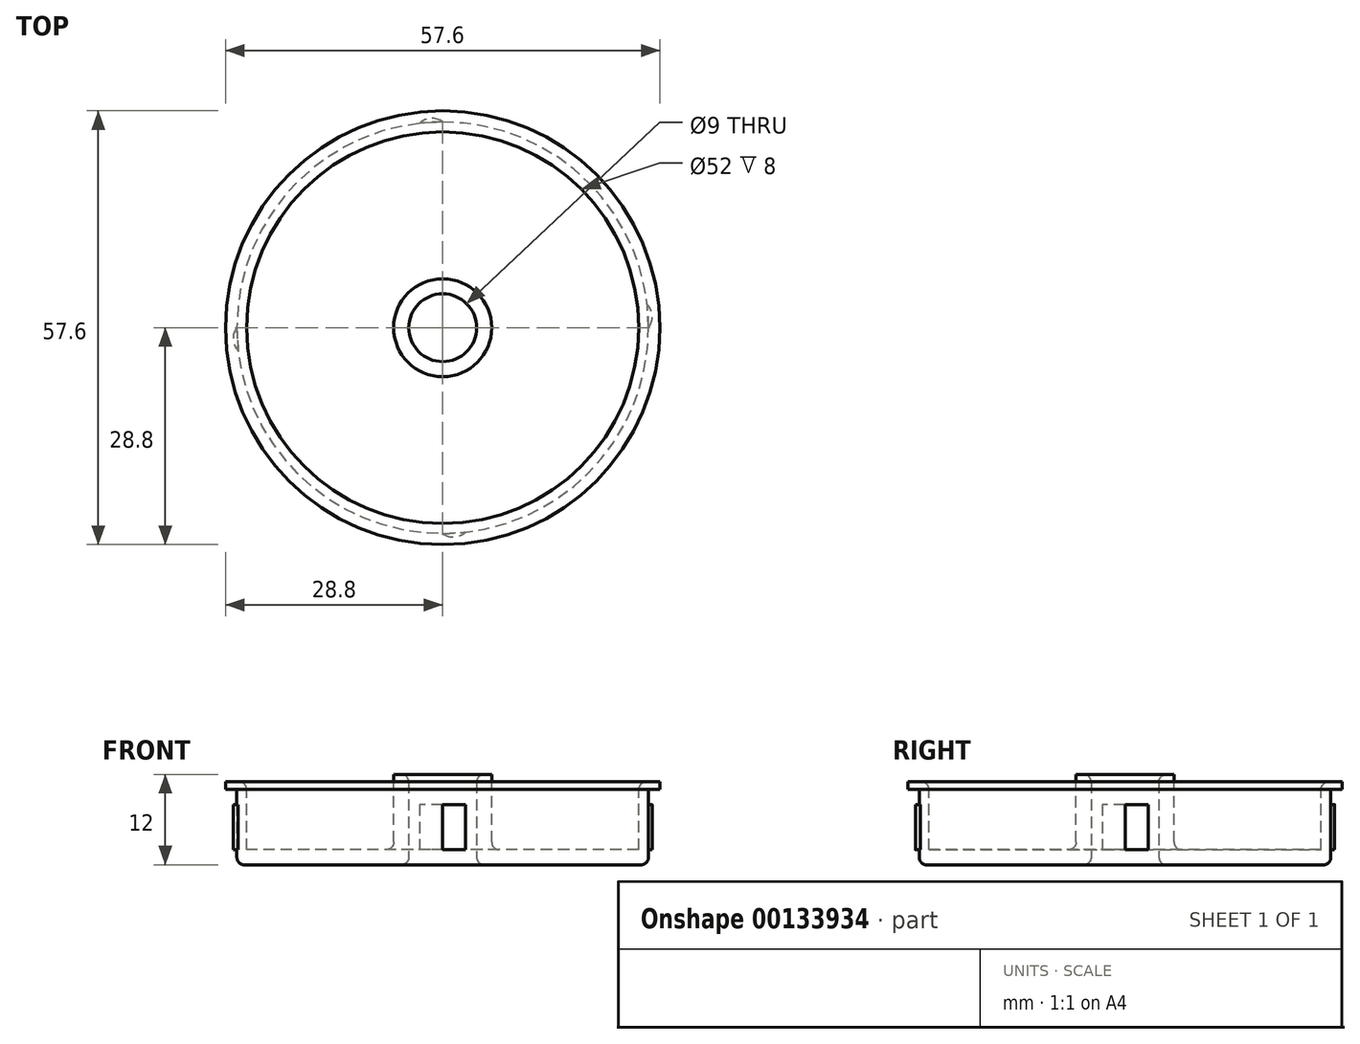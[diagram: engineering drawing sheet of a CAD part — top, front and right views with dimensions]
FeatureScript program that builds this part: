
annotation { "Feature Type Name" : "Feature", "Feature Type Description" : "" }
export const myFeature = defineFeature(function(context is Context, id is Id, definition is map)
    precondition{}
    {
        {
            var Q0;
            Q0=qCreatedBy(makeId("Top.planeOp"),FACE);
            var sketch = newSketch(context, id + "F0", { "sketchPlane" : qUnion([Q0])});
            skCircle(sketch, "E0", {"center": v(0, 0) * mm, "radius": 27.3 * mm});
            skCircle(sketch, "E1", {"center": v(0, 0) * mm, "radius": 4.5 * mm});
            skSolve(sketch);
        }
        {
            var Q0;
            Q0 = qSketchRegion(id + "F0", true);
            extrude(context, id + "F1", {"entities" : qUnion([Q0]), "depth" : 10 * mm});
        }
        {
            var Q0;
            Q0=makeQuery(id+"F1.opExtrude","CAP_FACE",FACE,{"disambiguationData":[OSD([sQuery(id+"F0.wireOp",EDGE,"E0"),sQuery(id+"F0.wireOp",EDGE,"E1")])],"isStart":false});
            var sketch = newSketch(context, id + "F2", { "sketchPlane" : qUnion([Q0])});
            skCircle(sketch, "E2.0", {"center": v(0, 0) * mm, "radius": 26 * mm});
            skCircle(sketch, "E3.0", {"center": v(0, 0) * mm, "radius": 6.5 * mm});
            skSolve(sketch);
        }
        {
            var Q0;
            Q0 = qSketchRegion(id + "F2", true);
            extrude(context, id + "F3", {"entities" : qUnion([Q0]), "operationType" : NewBodyOperationType.REMOVE, "oppositeDirection" : true, "depth" : 8 * mm});
        }
        {
            var Q0;
            {var subQ0=sQuery(id+"F0.wireOp",EDGE,"E0");Q0=makeQuery(id+"F3.boolean.opBoolean","SPLIT",FACE,{"disambiguationData":[TD([makeQuery(id+"F1.opExtrude","SWEPT_FACE",FACE,{"disambiguationData":[OSD([subQ0])]})])],"derivedFrom":makeQuery(id+"F1.opExtrude","CAP_FACE",FACE,{"disambiguationData":[OSD([subQ0,sQuery(id+"F0.wireOp",EDGE,"E1")])],"isStart":false})});}
            var sketch = newSketch(context, id + "F4", { "sketchPlane" : qUnion([Q0])});
            skCircle(sketch, "E4.0", {"center": v(0, 0) * mm, "radius": 28.8 * mm});
            skSolve(sketch);
        }
        {
            var Q0;
            Q0=makeQuery(id+"F4.imprint","IMPRINT",FACE,{"disambiguationData":[TD([[makeQuery(id+"F4.imprint","IMPRINT",EDGE,{"derivedFrom":sQuery(id+"F4.wireOp",EDGE,"E4.0")}),1.0]])]});
            var Q1;
            Q1=makeQuery(id+"F4.imprint","IMPRINT",FACE,{"disambiguationData":[TD([[makeQuery(id+"F4.imprint","IMPRINT",EDGE,{"derivedFrom":makeQuery(id+"F1.opExtrude","CAP_EDGE",EDGE,{"disambiguationData":[OSD([sQuery(id+"F0.wireOp",EDGE,"E0")])],"isStart":false})}),1.0]])]});
            extrude(context, id + "F5", {"entities" : qUnion([Q0, Q1]), "depth" : 1 * mm});
        }
        {
            var Q0;
            {var subQ0=sQuery(id+"F0.wireOp",EDGE,"E1");Q0=makeQuery(id+"F3.boolean.opBoolean","SPLIT",FACE,{"disambiguationData":[TD([makeQuery(id+"F1.opExtrude","SWEPT_FACE",FACE,{"disambiguationData":[OSD([subQ0])]})])],"derivedFrom":makeQuery(id+"F1.opExtrude","CAP_FACE",FACE,{"disambiguationData":[OSD([sQuery(id+"F0.wireOp",EDGE,"E0"),subQ0])],"isStart":false})});}
            var sketch = newSketch(context, id + "F6", { "sketchPlane" : qUnion([Q0])});
            skSolve(sketch);
        }
        {
            var Q0;
            Q0=makeQuery(id+"F6.imprint","IMPRINT",FACE,{"disambiguationData":[TD([[makeQuery(id+"F6.imprint","IMPRINT",EDGE,{"derivedFrom":makeQuery(id+"F1.opExtrude","CAP_EDGE",EDGE,{"disambiguationData":[OSD([sQuery(id+"F0.wireOp",EDGE,"E1")])],"isStart":false})}),-1.0]])]});
            extrude(context, id + "F7", {"entities" : qUnion([Q0]), "operationType" : NewBodyOperationType.ADD, "depth" : 2 * mm});
        }
        {
            var Q0;
            Q0=makeQuery(id+"F1.opExtrude","CAP_EDGE",EDGE,{"disambiguationData":[OSD([sQuery(id+"F0.wireOp",EDGE,"E1")])],"isStart":true});
            var Q1;
            Q1=makeQuery(id+"F7.opExtrude","CAP_EDGE",EDGE,{"disambiguationData":[OSD([sQuery(id+"F0.wireOp",EDGE,"E1")])],"isStart":false});
            var Q2;
            Q2=makeQuery(id+"F5.opExtrude","CAP_EDGE",EDGE,{"disambiguationData":[OSD([sQuery(id+"F2.wireOp",EDGE,"E2.0")])],"isStart":false});
            var Q3;
            Q3=makeQuery(id+"F3.boolean.opBoolean","COPY",EDGE,{"derivedFrom":makeQuery(id+"F3.opExtrude","CAP_EDGE",EDGE,{"disambiguationData":[OSD([sQuery(id+"F2.wireOp",EDGE,"E3.0")])],"isStart":false})});
            fillet(context, id + "F8", {"entities" : qUnion([Q0, Q1, Q2, Q3]), "radius" : 1 * mm, "tangentPropagation" : true, "allowEdgeOverflow" : false});
        }
        {
            var Q0;
            Q0=makeQuery(id+"F1.opExtrude","CAP_FACE",FACE,{"disambiguationData":[OSD([sQuery(id+"F0.wireOp",EDGE,"E0"),sQuery(id+"F0.wireOp",EDGE,"E1")])],"isStart":true});
            var sketch = newSketch(context, id + "F9", { "sketchPlane" : qUnion([Q0])});
            skArc(sketch, "E5", {"start": v(-27.13, 3.05) * mm, "mid": v(-27.79, 1.56) * mm, "end": v(-27.3, 0) * mm});
            skPoint(sketch, "E5.first.point", {"position": v(-27.3, 0) * mm});
            skPoint(sketch, "E5.second.point", {"position": v(-27.13, 3.05) * mm});
            skArc(sketch, "E6.1.0", {"start": v(-3.05, -27.13) * mm, "mid": v(-1.56, -27.79) * mm, "end": v(0, -27.3) * mm});
            skArc(sketch, "E6.2.0", {"start": v(27.13, -3.05) * mm, "mid": v(27.79, -1.56) * mm, "end": v(27.3, 0) * mm});
            skArc(sketch, "E6.3.0", {"start": v(3.05, 27.13) * mm, "mid": v(1.56, 27.79) * mm, "end": v(0, 27.3) * mm});
            skPoint(sketch, "E6.center", {"position": v(0, 0) * mm});
            skSolve(sketch);
        }
        {
            var Q0;
            {var subQ0=sQuery(id+"F9.wireOp",EDGE,"E6.2.0");Q0=makeQuery(id+"F9.imprint","IMPRINT",FACE,{"disambiguationData":[TD([[makeQuery(id+"F9.imprint","IMPRINT",EDGE,{"derivedFrom":subQ0}),1.0]])]});}
            var Q1;
            {var subQ0=sQuery(id+"F9.wireOp",EDGE,"E5");Q1=makeQuery(id+"F9.imprint","IMPRINT",FACE,{"disambiguationData":[TD([[makeQuery(id+"F9.imprint","IMPRINT",EDGE,{"derivedFrom":subQ0}),1.0]])]});}
            var Q2;
            {var subQ0=sQuery(id+"F9.wireOp",EDGE,"E6.3.0");Q2=makeQuery(id+"F9.imprint","IMPRINT",FACE,{"disambiguationData":[TD([[makeQuery(id+"F9.imprint","IMPRINT",EDGE,{"derivedFrom":subQ0}),1.0]])]});}
            var Q3;
            {var subQ0=sQuery(id+"F9.wireOp",EDGE,"E6.1.0");Q3=makeQuery(id+"F9.imprint","IMPRINT",FACE,{"disambiguationData":[TD([[makeQuery(id+"F9.imprint","IMPRINT",EDGE,{"derivedFrom":subQ0}),1.0]])]});}
            extrude(context, id + "F10", {"entities" : qUnion([Q0, Q1, Q2, Q3]), "operationType" : NewBodyOperationType.ADD, "oppositeDirection" : true, "depth" : 8 * mm, "hasSecondDirection" : true, "secondDirectionOppositeDirection" : true, "secondDirectionDepth" : 2 * mm});
        }
        {
            var Q0;
            Q0=makeQuery(id+"F1.opExtrude","CAP_EDGE",EDGE,{"disambiguationData":[OSD([sQuery(id+"F0.wireOp",EDGE,"E0")])],"isStart":true});
            fillet(context, id + "F11", {"entities" : qUnion([Q0]), "radius" : 1 * mm, "tangentPropagation" : true, "allowEdgeOverflow" : false});
        }
    });
